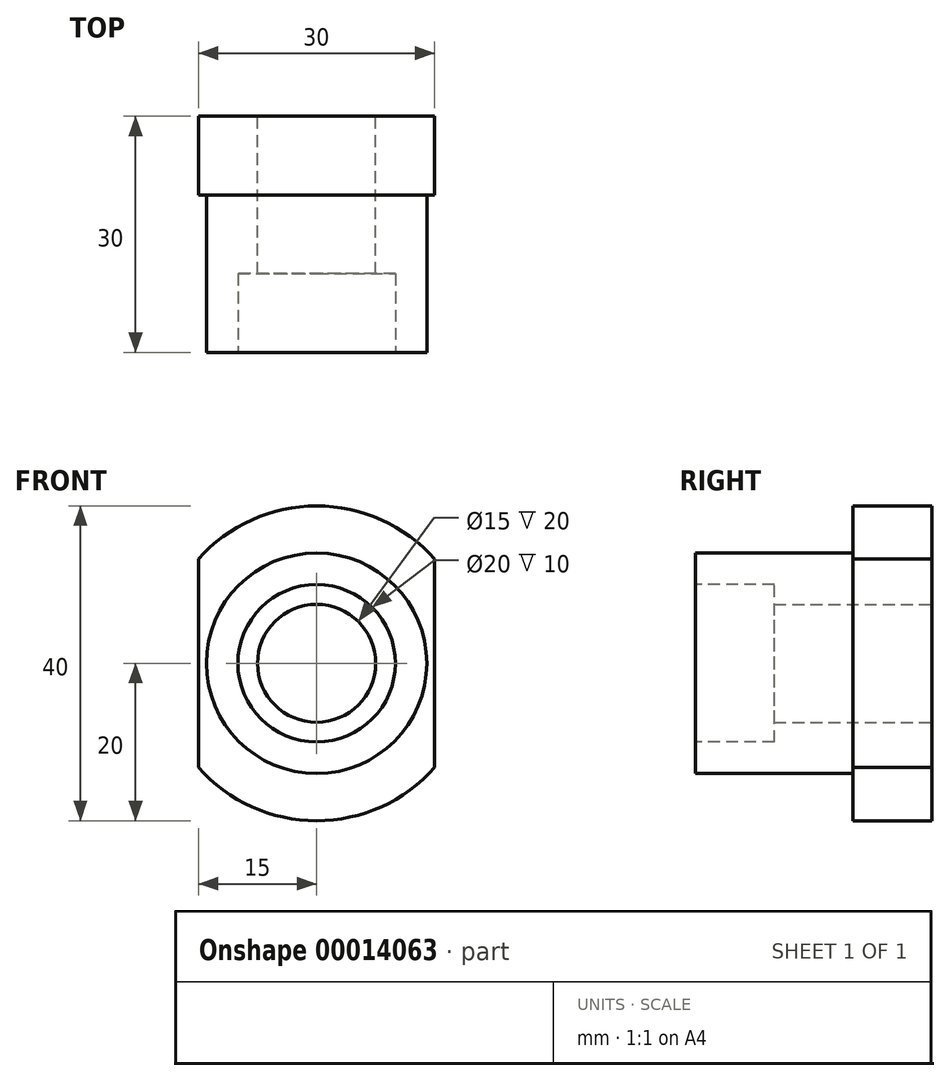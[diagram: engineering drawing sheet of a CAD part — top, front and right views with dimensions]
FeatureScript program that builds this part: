
annotation { "Feature Type Name" : "Feature", "Feature Type Description" : "" }
export const myFeature = defineFeature(function(context is Context, id is Id, definition is map)
    precondition{}
    {
        {
            var Q0;
            Q0=qCreatedBy(makeId("Front.planeOp"),FACE);
            var sketch = newSketch(context, id + "F0", { "sketchPlane" : qUnion([Q0])});
            skCircle(sketch, "E0", {"center": v(0, 0) * mm, "radius": 20 * mm});
            skCircle(sketch, "E1", {"center": v(0, 0) * mm, "radius": 7.5 * mm});
            skSolve(sketch);
        }
        {
            var Q0;
            Q0=makeQuery(id+"F0.imprint","IMPRINT",FACE,{"disambiguationData":[TD([[makeQuery(id+"F0.imprint","IMPRINT",EDGE,{"derivedFrom":sQuery(id+"F0.wireOp",EDGE,"E0")}),1.0]])]});
            extrude(context, id + "F1", {"entities" : qUnion([Q0]), "depth" : 10 * mm});
        }
        {
            var Q0;
            Q0=makeQuery(id+"F1.opExtrude","CAP_FACE",FACE,{"disambiguationData":[OSD([sQuery(id+"F0.wireOp",EDGE,"E0"),sQuery(id+"F0.wireOp",EDGE,"E1")])],"isStart":false});
            var sketch = newSketch(context, id + "F2", { "sketchPlane" : qUnion([Q0])});
            skCircle(sketch, "E2", {"center": v(0, 0) * mm, "radius": 14 * mm});
            skCircle(sketch, "E3.0", {"center": v(0, 0) * mm, "radius": 7.5 * mm});
            skSolve(sketch);
        }
        {
            var Q0;
            Q0 = qSketchRegion(id + "F2", true);
            extrude(context, id + "F3", {"entities" : qUnion([Q0]), "operationType" : NewBodyOperationType.ADD, "depth" : 20 * mm});
        }
        {
            var Q0;
            Q0=makeQuery(id+"F3.opExtrude","CAP_FACE",FACE,{"disambiguationData":[OSD([sQuery(id+"F2.wireOp",EDGE,"E2"),sQuery(id+"F2.wireOp",EDGE,"E3.0")])],"isStart":false});
            var sketch = newSketch(context, id + "F4", { "sketchPlane" : qUnion([Q0])});
            skCircle(sketch, "E4", {"center": v(0, 0) * mm, "radius": 10 * mm});
            skSolve(sketch);
        }
        {
            var Q0;
            Q0 = qSketchRegion(id + "F4", true);
            extrude(context, id + "F5", {"entities" : qUnion([Q0]), "operationType" : NewBodyOperationType.REMOVE, "oppositeDirection" : true, "depth" : 10 * mm});
        }
        {
            var Q0;
            Q0=makeQuery(id+"F1.opExtrude","CAP_FACE",FACE,{"disambiguationData":[OSD([sQuery(id+"F0.wireOp",EDGE,"E0"),sQuery(id+"F0.wireOp",EDGE,"E1")])],"isStart":true});
            var sketch = newSketch(context, id + "F6", { "sketchPlane" : qUnion([Q0])});
            skLineSegment(sketch, "E5.rect.bottom", {"start": v(-15, -13.23) * mm, "end": v(15, -13.23) * mm});
            skLineSegment(sketch, "E5.rect.top", {"start": v(-15, 13.23) * mm, "end": v(15, 13.23) * mm});
            skLineSegment(sketch, "E5.rect.left", {"start": v(-15, -13.23) * mm, "end": v(-15, 13.23) * mm});
            skLineSegment(sketch, "E5.rect.right", {"start": v(15, -13.23) * mm, "end": v(15, 13.23) * mm});
            skPoint(sketch, "E5.rect.middle", {"position": v(0, 0) * mm});
            skSolve(sketch);
        }
        {
            var Q0;
            {var subQ1=sQuery(id+"F6.wireOp",EDGE,"E5.rect.left");Q0=makeQuery(id+"F6.imprint","IMPRINT",FACE,{"disambiguationData":[TD([[makeQuery(id+"F6.imprint","IMPRINT",EDGE,{"derivedFrom":subQ1}),1.0]])]});}
            var Q1;
            {var subQ1=sQuery(id+"F6.wireOp",EDGE,"E5.rect.right");Q1=makeQuery(id+"F6.imprint","IMPRINT",FACE,{"disambiguationData":[TD([[makeQuery(id+"F6.imprint","IMPRINT",EDGE,{"derivedFrom":subQ1}),-1.0]])]});}
            extrude(context, id + "F7", {"entities" : qUnion([Q0, Q1]), "operationType" : NewBodyOperationType.REMOVE, "oppositeDirection" : true, "depth" : 25 * mm});
        }
    });
